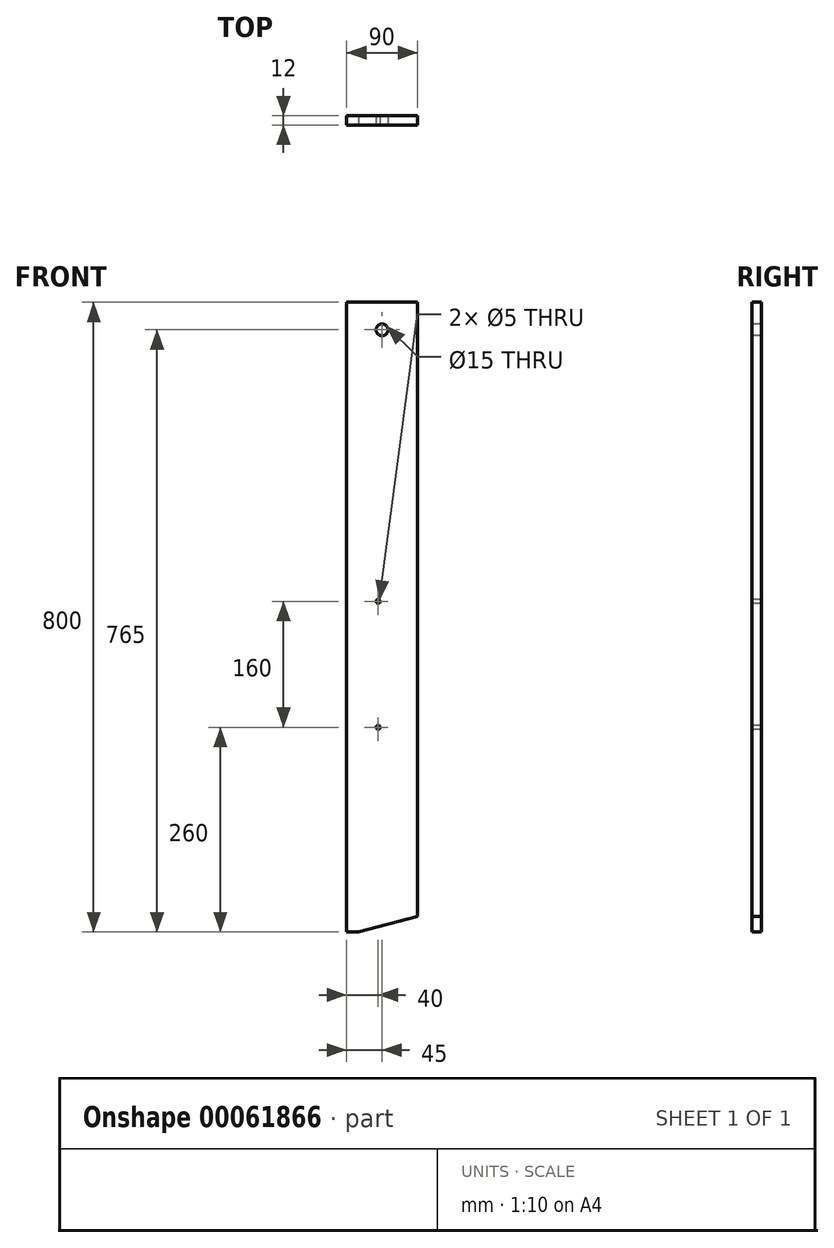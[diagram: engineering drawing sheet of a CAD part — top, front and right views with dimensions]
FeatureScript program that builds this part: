
annotation { "Feature Type Name" : "Feature", "Feature Type Description" : "" }
export const myFeature = defineFeature(function(context is Context, id is Id, definition is map)
    precondition{}
    {
        {
            var Q0;
            Q0=qCreatedBy(makeId("Front.planeOp"),FACE);
            var sketch = newSketch(context, id + "F0", { "sketchPlane" : qUnion([Q0])});
            skLineSegment(sketch, "E0.bottom", {"start": v(0, 0) * mm, "end": v(90, 0) * mm});
            skLineSegment(sketch, "E0.top", {"start": v(0, -800) * mm, "end": v(90, -800) * mm});
            skLineSegment(sketch, "E0.left", {"start": v(0, 0) * mm, "end": v(0, -800) * mm});
            skLineSegment(sketch, "E0.right", {"start": v(90, 0) * mm, "end": v(90, -800) * mm});
            skSolve(sketch);
        }
        {
            var Q0;
            Q0 = qSketchRegion(id + "F0", true);
            extrude(context, id + "F1", {"entities" : qUnion([Q0]), "depth" : 12 * mm});
        }
        {
            var Q0;
            Q0=makeQuery(id+"F1.opExtrude","CAP_FACE",FACE,{"disambiguationData":[OSD([sQuery(id+"F0.wireOp",EDGE,"E0.bottom"),sQuery(id+"F0.wireOp",EDGE,"E0.top"),sQuery(id+"F0.wireOp",EDGE,"E0.left"),sQuery(id+"F0.wireOp",EDGE,"E0.right")])],"isStart":false});
            var sketch = newSketch(context, id + "F2", { "sketchPlane" : qUnion([Q0])});
            skPoint(sketch, "E1.center.orphan", {"position": v(45, -35) * mm});
            skSolve(sketch);
        }
        {
            var Q0;
            Q0=sQuery(id+"F2.wireOp",VERTEX,"E1.center.orphan");
            var Q1;
            Q1=makeQuery(id+"F1.opExtrude","SWEPT_BODY",BODY,{"disambiguationData":[OSD([sQuery(id+"F0.wireOp",EDGE,"E0.bottom"),sQuery(id+"F0.wireOp",EDGE,"E0.top"),sQuery(id+"F0.wireOp",EDGE,"E0.left"),sQuery(id+"F0.wireOp",EDGE,"E0.right")])]});
            hole(context, id + "F3", {"style" : HoleStyle.SIMPLE, "holeDiameter" : 15 * mm, "endStyle" : HoleEndStyle.THROUGH, "locations" : qUnion([Q0]), "scope" : qUnion([Q1])});
        }
        {
            var Q0;
            Q0=makeQuery(id+"F1.opExtrude","SWEPT_EDGE",EDGE,{"disambiguationData":[OSD([sQuery(id+"F0.wireOp",EDGE,"E0.top"),sQuery(id+"F0.wireOp",EDGE,"E0.right")])]});
            chamfer(context, id + "F4", {"entities" : qUnion([Q0]), "chamferType" : ChamferType.OFFSET_ANGLE, "width" : 20 * mm, "oppositeDirection" : false, "angle" : 75 * degree, "tangentPropagation" : true});
        }
        {
            var Q0;
            Q0=makeQuery(id+"F1.opExtrude","CAP_FACE",FACE,{"disambiguationData":[OSD([sQuery(id+"F0.wireOp",EDGE,"E0.bottom"),sQuery(id+"F0.wireOp",EDGE,"E0.top"),sQuery(id+"F0.wireOp",EDGE,"E0.left"),sQuery(id+"F0.wireOp",EDGE,"E0.right")])],"isStart":false});
            var sketch = newSketch(context, id + "F5", { "sketchPlane" : qUnion([Q0])});
            skPoint(sketch, "E2", {"position": v(40, -380) * mm});
            skPoint(sketch, "E3", {"position": v(40, -540) * mm});
            skSolve(sketch);
        }
        {
            var Q0;
            Q0=sQuery(id+"F5.wireOp",VERTEX,"E2");
            var Q1;
            Q1=sQuery(id+"F5.wireOp",VERTEX,"E3");
            var Q2;
            Q2=makeQuery(id+"F1.opExtrude","SWEPT_BODY",BODY,{"disambiguationData":[OSD([sQuery(id+"F0.wireOp",EDGE,"E0.bottom"),sQuery(id+"F0.wireOp",EDGE,"E0.top"),sQuery(id+"F0.wireOp",EDGE,"E0.left"),sQuery(id+"F0.wireOp",EDGE,"E0.right")])]});
            hole(context, id + "F6", {"style" : HoleStyle.SIMPLE, "holeDiameter" : 5 * mm, "endStyle" : HoleEndStyle.THROUGH, "locations" : qUnion([Q0, Q1]), "scope" : qUnion([Q2])});
        }
    });
